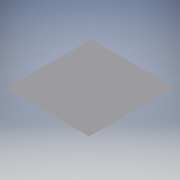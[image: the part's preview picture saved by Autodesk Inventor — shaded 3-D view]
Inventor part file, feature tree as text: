
AUTODESK INVENTOR PART (.ipt)
format: ipt  version: 2018 (Build 220112000, 112)  size: 96,768 bytes
history: native  units: mm
features: extrude x1, chamfer x1, sketch x1
ambient origin geometry x8: Origin, YZ Plane, XZ Plane, XY Plane, X Axis, Y Axis, Z Axis, Center Point
bodies: Volumenkörper1 (feature_tree)
feature tree (3):
  extrude  "Extrusion1"  Depth=20.0mm
  chamfer  "Fase1"  Distance=20.0mm
  sketch  "Skizze1"  dims[d0=440.0mm d1=450.0mm d2=20.0mm d3=0.0mm d4=20.0mm d5=2.0mm d6=45.0deg]
